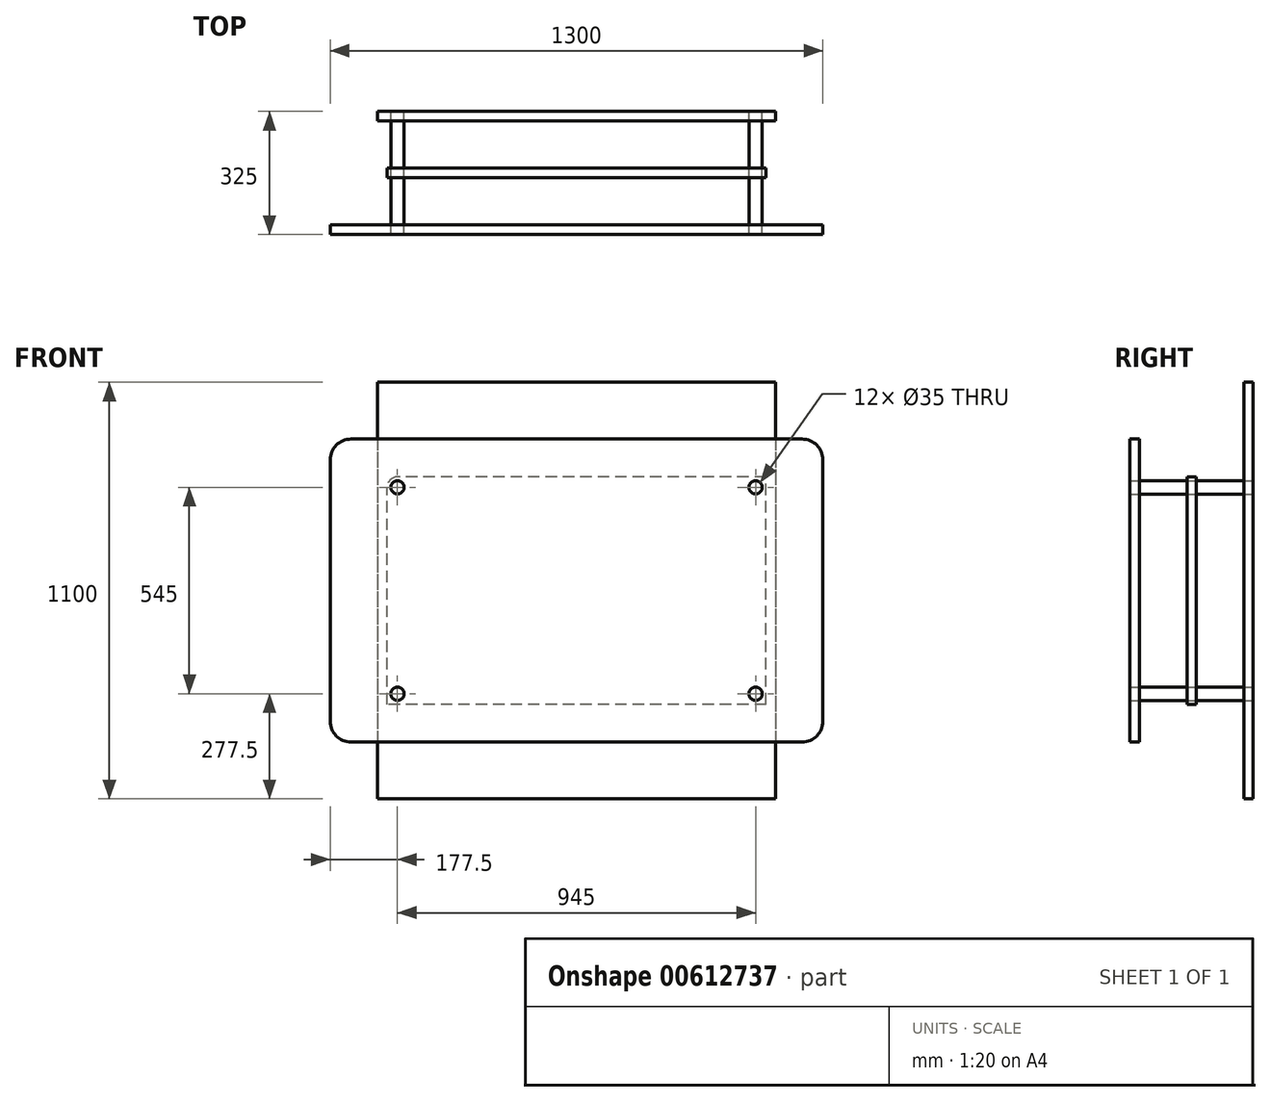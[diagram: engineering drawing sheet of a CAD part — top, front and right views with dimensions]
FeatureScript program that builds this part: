
annotation { "Feature Type Name" : "Feature", "Feature Type Description" : "" }
export const myFeature = defineFeature(function(context is Context, id is Id, definition is map)
    precondition{}
    {
        {
            var Q0;
            Q0=qCreatedBy(makeId("Front.planeOp"),FACE);
            var sketch = newSketch(context, id + "F0", { "sketchPlane" : qUnion([Q0])});
            skLineSegment(sketch, "E0.bottom", {"start": v(500, -300) * mm, "end": v(-500, -300) * mm});
            skLineSegment(sketch, "E0.top", {"start": v(500, 300) * mm, "end": v(-472.5, 300) * mm});
            skLineSegment(sketch, "E0.left", {"start": v(500, -300) * mm, "end": v(500, 300) * mm});
            skLineSegment(sketch, "E0.right", {"start": v(-500, -300) * mm, "end": v(-500, 272.5) * mm});
            skPoint(sketch, "E0.middle", {"position": v(0, 0) * mm});
            skCircle(sketch, "E1", {"center": v(-472.5, 272.5) * mm, "radius": 17.5 * mm});
            skCircle(sketch, "E2", {"center": v(-472.5, -272.5) * mm, "radius": 17.5 * mm});
            skCircle(sketch, "E3", {"center": v(472.5, -272.5) * mm, "radius": 17.5 * mm});
            skCircle(sketch, "E4", {"center": v(472.5, 272.5) * mm, "radius": 17.5 * mm});
            skLineSegment(sketch, "E5.0", {"start": v(490, 290) * mm, "end": v(-490, 290) * mm, "construction": true});
            skLineSegment(sketch, "E5.1", {"start": v(490, -290) * mm, "end": v(490, 290) * mm, "construction": true});
            skLineSegment(sketch, "E5.2", {"start": v(490, -290) * mm, "end": v(-490, -290) * mm, "construction": true});
            skLineSegment(sketch, "E5.3", {"start": v(-490, -290) * mm, "end": v(-490, 290) * mm, "construction": true});
            skArc(sketch, "E6", {"start": v(-472.5, 300) * mm, "mid": v(-491.95, 291.95) * mm, "end": v(-500, 272.5) * mm});
            skPoint(sketch, "E7.orphan", {"position": v(-500, 300) * mm});
            skSolve(sketch);
        }
        {
            var Q0;
            Q0=makeQuery(id+"F0.imprint","IMPRINT",FACE,{"disambiguationData":[TD([[makeQuery(id+"F0.imprint","IMPRINT",EDGE,{"derivedFrom":sQuery(id+"F0.wireOp",EDGE,"E0.bottom")}),-1.0]])]});
            extrude(context, id + "F1", {"entities" : qUnion([Q0]), "depth" : 25 * mm, "offsetDistance" : 25 * mm});
        }
        {
            var Q0;
            Q0=qCreatedBy(makeId("Front.planeOp"),FACE);
            cPlane(context, id + "F2", {"entities" : qUnion([Q0]), "cplaneType" : CPlaneType.OFFSET, "offset" : 150 * mm, "width" : 150 * mm, "height" : 150 * mm});
        }
        {
            var Q0;
            Q0=qCreatedBy(id+"F2.planeOp",FACE);
            var sketch = newSketch(context, id + "F3", { "sketchPlane" : qUnion([Q0])});
            skLineSegment(sketch, "E8.bottom", {"start": v(595, -400) * mm, "end": v(-595, -400) * mm});
            skLineSegment(sketch, "E8.top", {"start": v(595, 400) * mm, "end": v(-595, 400) * mm});
            skLineSegment(sketch, "E8.left", {"start": v(650, -345) * mm, "end": v(650, 345) * mm});
            skLineSegment(sketch, "E8.right", {"start": v(-650, -345) * mm, "end": v(-650, 345) * mm});
            skPoint(sketch, "E8.middle", {"position": v(0, 0) * mm});
            skCircle(sketch, "E9.0", {"center": v(-472.5, 272.5) * mm, "radius": 17.5 * mm});
            skCircle(sketch, "E10.0", {"center": v(-472.5, -272.5) * mm, "radius": 17.5 * mm});
            skCircle(sketch, "E11.0", {"center": v(472.5, 272.5) * mm, "radius": 17.5 * mm});
            skCircle(sketch, "E12.0", {"center": v(472.5, -272.5) * mm, "radius": 17.5 * mm});
            skPoint(sketch, "E13.visualSharp", {"position": v(-650, 400) * mm});
            skArc(sketch, "E13.filletArc", {"start": v(-595, 400) * mm, "mid": v(-633.9, 383.9) * mm, "end": v(-650, 345) * mm});
            skPoint(sketch, "E14.visualSharp", {"position": v(650, 400) * mm});
            skArc(sketch, "E14.filletArc", {"start": v(650, 345) * mm, "mid": v(633.9, 383.9) * mm, "end": v(595, 400) * mm});
            skPoint(sketch, "E15.visualSharp", {"position": v(650, -400) * mm});
            skArc(sketch, "E15.filletArc", {"start": v(595, -400) * mm, "mid": v(633.9, -383.9) * mm, "end": v(650, -345) * mm});
            skPoint(sketch, "E16.visualSharp", {"position": v(-650, -400) * mm});
            skArc(sketch, "E16.filletArc", {"start": v(-650, -345) * mm, "mid": v(-633.9, -383.9) * mm, "end": v(-595, -400) * mm});
            skSolve(sketch);
        }
        {
            var Q0;
            Q0=makeQuery(id+"F3.imprint","IMPRINT",FACE,{"disambiguationData":[TD([[makeQuery(id+"F3.imprint","IMPRINT",EDGE,{"derivedFrom":sQuery(id+"F3.wireOp",EDGE,"E8.bottom")}),-1.0]])]});
            extrude(context, id + "F4", {"entities" : qUnion([Q0]), "depth" : 25 * mm, "offsetDistance" : 25 * mm});
        }
        {
            var Q0;
            Q0=qCreatedBy(makeId("Front.planeOp"),FACE);
            cPlane(context, id + "F5", {"entities" : qUnion([Q0]), "cplaneType" : CPlaneType.OFFSET, "offset" : 150 * mm, "oppositeDirection" : true, "width" : 150 * mm, "height" : 150 * mm});
        }
        {
            var Q0;
            Q0=qCreatedBy(id+"F5.planeOp",FACE);
            var sketch = newSketch(context, id + "F6", { "sketchPlane" : qUnion([Q0])});
            skLineSegment(sketch, "E17.bottom", {"start": v(525, 550) * mm, "end": v(-525, 550) * mm});
            skLineSegment(sketch, "E17.top", {"start": v(525, -550) * mm, "end": v(-525, -550) * mm});
            skLineSegment(sketch, "E17.left", {"start": v(525, 550) * mm, "end": v(525, -550) * mm});
            skLineSegment(sketch, "E17.right", {"start": v(-525, 550) * mm, "end": v(-525, -550) * mm});
            skPoint(sketch, "E17.middle", {"position": v(0, 0) * mm});
            skCircle(sketch, "E18.0", {"center": v(-472.5, 272.5) * mm, "radius": 17.5 * mm});
            skCircle(sketch, "E19.0", {"center": v(-472.5, -272.5) * mm, "radius": 17.5 * mm});
            skCircle(sketch, "E20.0", {"center": v(472.5, -272.5) * mm, "radius": 17.5 * mm});
            skCircle(sketch, "E21.0", {"center": v(472.5, 272.5) * mm, "radius": 17.5 * mm});
            skSolve(sketch);
        }
        {
            var Q0;
            Q0=makeQuery(id+"F6.imprint","IMPRINT",FACE,{"disambiguationData":[TD([[makeQuery(id+"F6.imprint","IMPRINT",EDGE,{"derivedFrom":sQuery(id+"F6.wireOp",EDGE,"E17.bottom")}),1.0]])]});
            extrude(context, id + "F7", {"entities" : qUnion([Q0]), "depth" : 25 * mm, "offsetDistance" : 25 * mm});
        }
        {
            var Q0;
            Q0=qCreatedBy(id+"F5.planeOp",FACE);
            var sketch = newSketch(context, id + "F8", { "sketchPlane" : qUnion([Q0])});
            skCircle(sketch, "E22.0", {"center": v(-472.5, 272.5) * mm, "radius": 17.5 * mm});
            skCircle(sketch, "E23.0", {"center": v(-472.5, -272.5) * mm, "radius": 17.5 * mm});
            skCircle(sketch, "E24.0", {"center": v(472.5, -272.5) * mm, "radius": 17.5 * mm});
            skCircle(sketch, "E25.0", {"center": v(472.5, 272.5) * mm, "radius": 17.5 * mm});
            skSolve(sketch);
        }
        {
            var Q0;
            Q0 = qSketchRegion(id + "F8", true);
            var Q1;
            Q1=makeQuery(id+"F4.opExtrude","CAP_FACE",FACE,{"disambiguationData":[OSD([sQuery(id+"F3.wireOp",EDGE,"E8.bottom"),sQuery(id+"F3.wireOp",EDGE,"E8.top"),sQuery(id+"F3.wireOp",EDGE,"E8.left"),sQuery(id+"F3.wireOp",EDGE,"E8.right"),sQuery(id+"F3.wireOp",EDGE,"E9.0"),sQuery(id+"F3.wireOp",EDGE,"E10.0"),sQuery(id+"F3.wireOp",EDGE,"E11.0"),sQuery(id+"F3.wireOp",EDGE,"E12.0"),sQuery(id+"F3.wireOp",EDGE,"E13.filletArc"),sQuery(id+"F3.wireOp",EDGE,"E14.filletArc"),sQuery(id+"F3.wireOp",EDGE,"E15.filletArc"),sQuery(id+"F3.wireOp",EDGE,"E16.filletArc")])],"isStart":false});
            extrude(context, id + "F9", {"entities" : qUnion([Q0]), "endBound" : BoundingType.UP_TO_SURFACE, "depth" : 25 * mm, "endBoundEntityFace" : qUnion([Q1]), "offsetDistance" : 25 * mm});
        }
    });
